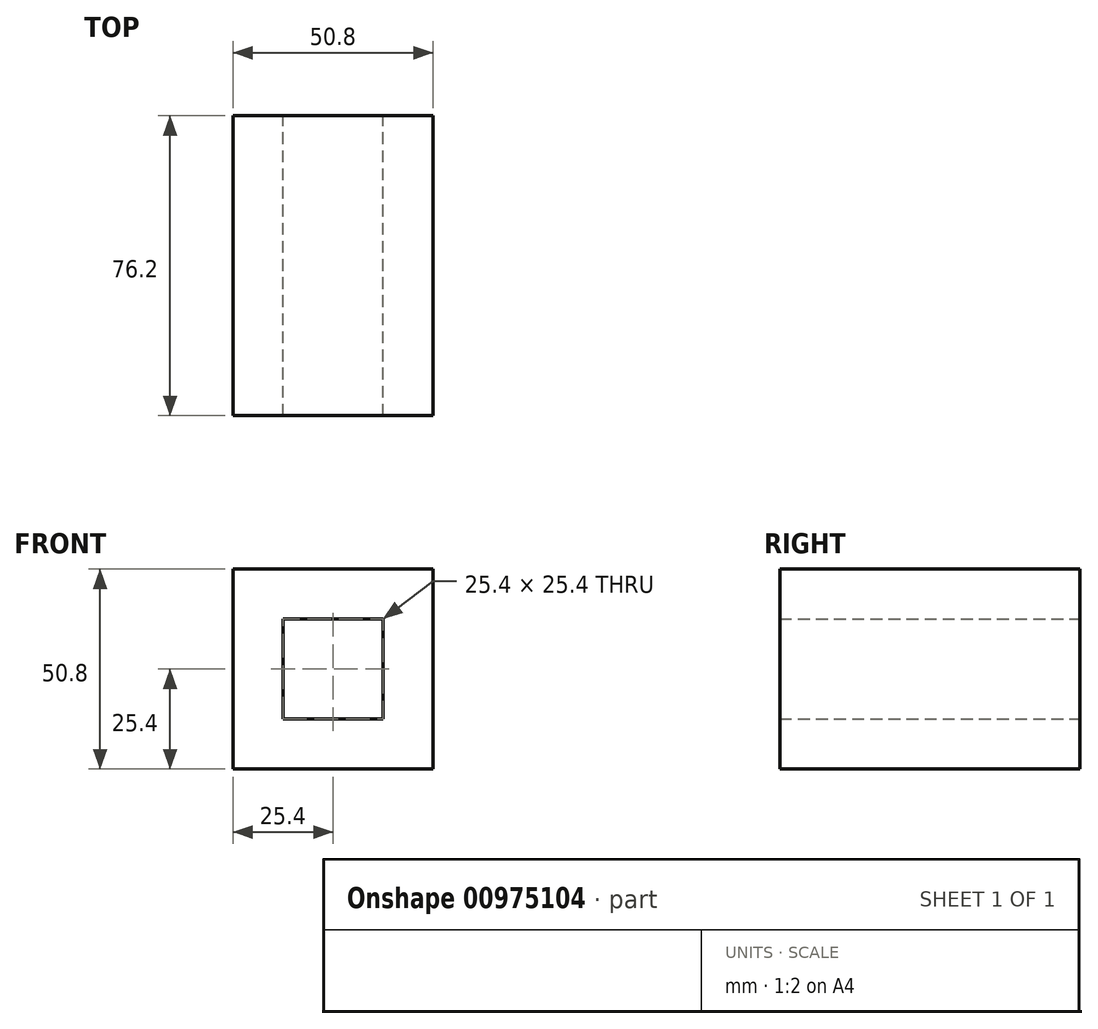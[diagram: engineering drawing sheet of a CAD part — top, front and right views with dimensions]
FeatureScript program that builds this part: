
annotation { "Feature Type Name" : "Feature", "Feature Type Description" : "" }
export const myFeature = defineFeature(function(context is Context, id is Id, definition is map)
    precondition{}
    {
        {
            var Q0;
            Q0=qCreatedBy(makeId("Front.planeOp"),FACE);
            var sketch = newSketch(context, id + "F0", { "sketchPlane" : qUnion([Q0])});
            skLineSegment(sketch, "E0.bottom", {"start": v(12.7, -12.7) * mm, "end": v(-12.7, -12.7) * mm});
            skLineSegment(sketch, "E0.top", {"start": v(12.7, 12.7) * mm, "end": v(-12.7, 12.7) * mm});
            skLineSegment(sketch, "E0.left", {"start": v(12.7, -12.7) * mm, "end": v(12.7, 12.7) * mm});
            skLineSegment(sketch, "E0.right", {"start": v(-12.7, -12.7) * mm, "end": v(-12.7, 12.7) * mm});
            skPoint(sketch, "E0.middle", {"position": v(0, 0) * mm});
            skLineSegment(sketch, "E1.bottom", {"start": v(25.4, -25.4) * mm, "end": v(-25.4, -25.4) * mm});
            skLineSegment(sketch, "E1.top", {"start": v(25.4, 25.4) * mm, "end": v(-25.4, 25.4) * mm});
            skLineSegment(sketch, "E1.left", {"start": v(25.4, -25.4) * mm, "end": v(25.4, 25.4) * mm});
            skLineSegment(sketch, "E1.right", {"start": v(-25.4, -25.4) * mm, "end": v(-25.4, 25.4) * mm});
            skSolve(sketch);
        }
        {
            var Q0;
            Q0=makeQuery(id+"F0.imprint","IMPRINT",FACE,{"disambiguationData":[TD([[makeQuery(id+"F0.imprint","IMPRINT",EDGE,{"derivedFrom":sQuery(id+"F0.wireOp",EDGE,"E0.bottom")}),1.0]])]});
            extrude(context, id + "F1", {"entities" : qUnion([Q0]), "endBound" : BoundingType.SYMMETRIC, "depth" : 76.2 * mm, "offsetDistance" : 25.4 * mm});
        }
    });
